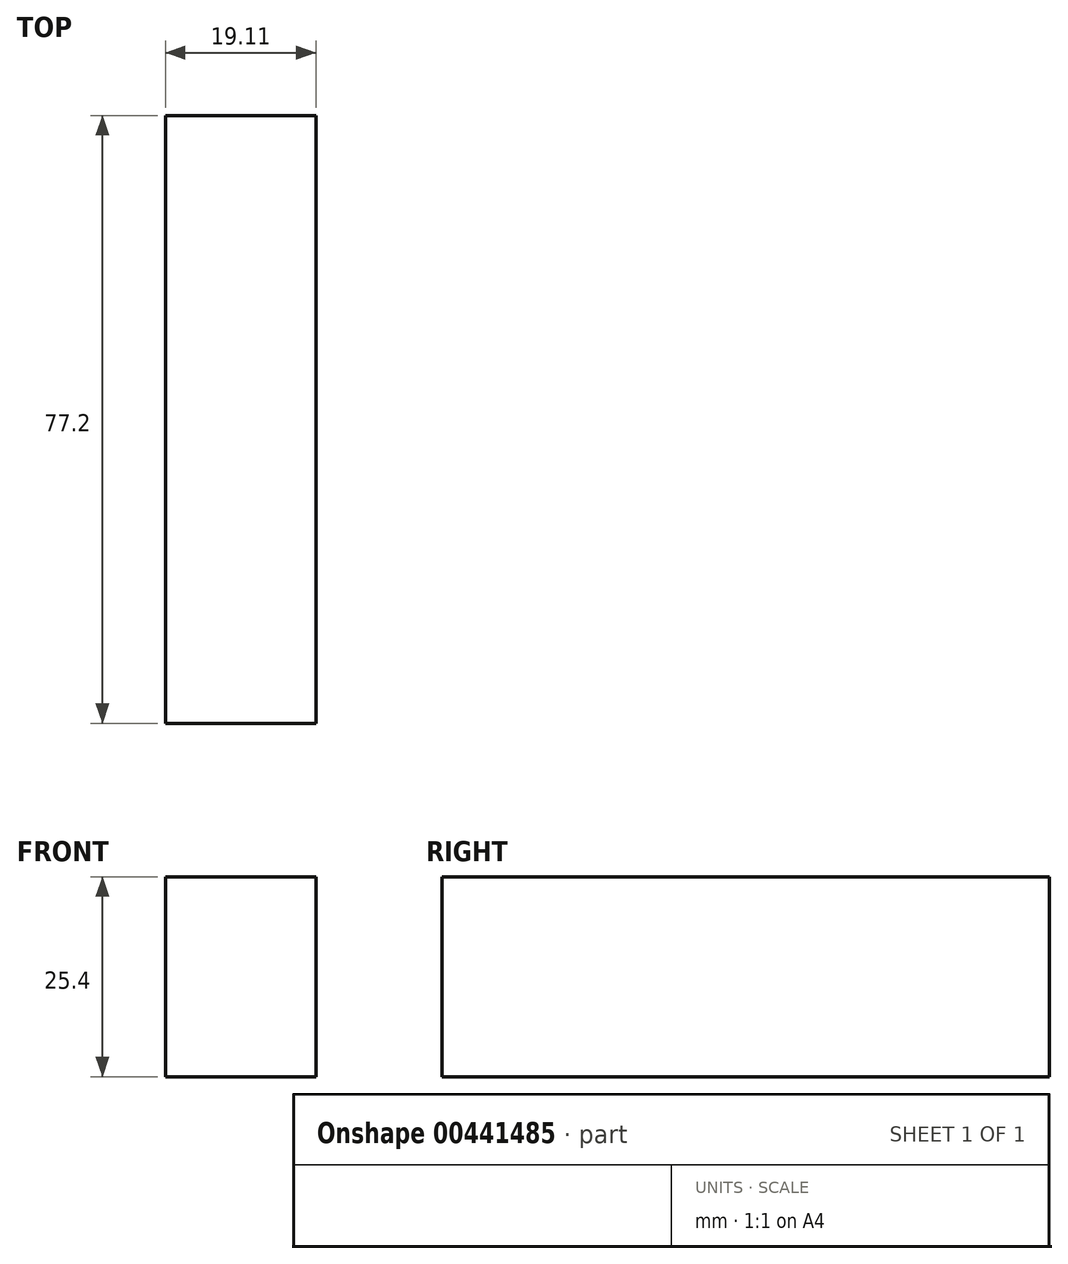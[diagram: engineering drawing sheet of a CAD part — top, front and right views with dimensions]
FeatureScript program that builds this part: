
annotation { "Feature Type Name" : "Feature", "Feature Type Description" : "" }
export const myFeature = defineFeature(function(context is Context, id is Id, definition is map)
    precondition{}
    {
        {
            var Q0;
            Q0=qCreatedBy(makeId("Top.planeOp"),FACE);
            var sketch = newSketch(context, id + "F0", { "sketchPlane" : qUnion([Q0])});
            skLineSegment(sketch, "E0.bottom", {"start": v(0, 41.04) * mm, "end": v(-19.11, 41.04) * mm});
            skLineSegment(sketch, "E0.top", {"start": v(0, -36.16) * mm, "end": v(-19.11, -36.16) * mm});
            skLineSegment(sketch, "E0.left", {"start": v(0, 41.04) * mm, "end": v(0, -36.16) * mm});
            skLineSegment(sketch, "E0.right", {"start": v(-19.11, 41.04) * mm, "end": v(-19.11, -36.16) * mm});
            skSolve(sketch);
        }
        {
            var Q0;
            Q0 = qSketchRegion(id + "F0", true);
            extrude(context, id + "F1", {"entities" : qUnion([Q0]), "depth" : 25.4 * mm});
        }
    });
